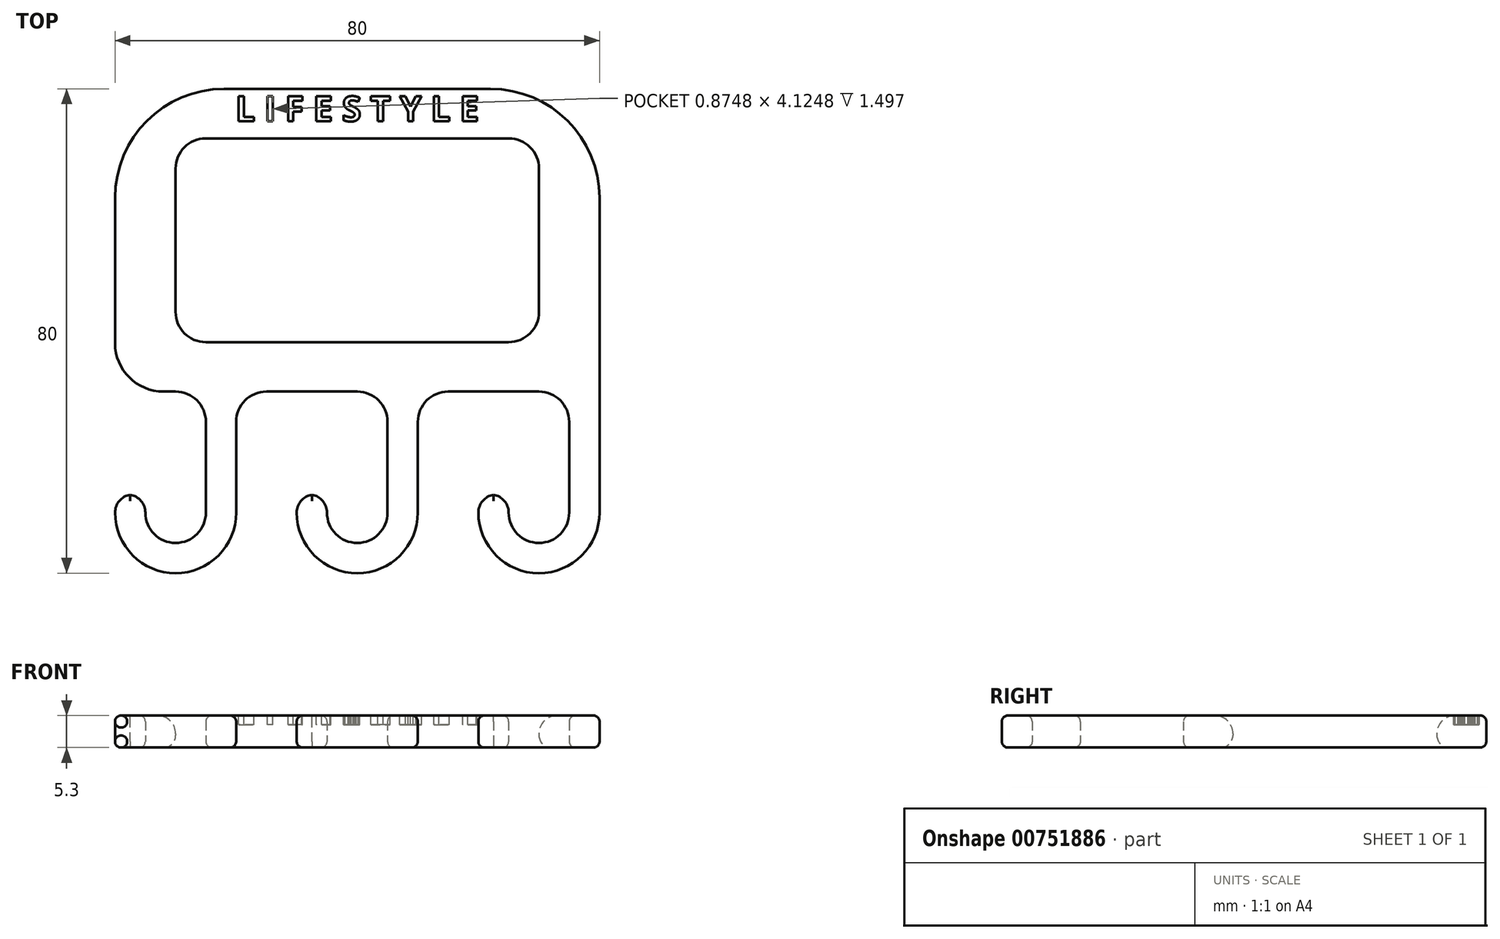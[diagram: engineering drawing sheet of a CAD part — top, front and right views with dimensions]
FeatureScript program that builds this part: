
annotation { "Feature Type Name" : "Feature", "Feature Type Description" : "" }
export const myFeature = defineFeature(function(context is Context, id is Id, definition is map)
    precondition{}
    {
        {
            var Q0;
            Q0=qCreatedBy(makeId("Top.planeOp"),FACE);
            var sketch = newSketch(context, id + "F0", { "sketchPlane" : qUnion([Q0])});
            skLineSegment(sketch, "E0.bottom", {"start": v(0, 0) * mm, "end": v(15, 0) * mm});
            skLineSegment(sketch, "E0.top", {"start": v(0, 50) * mm, "end": v(80, 50) * mm});
            skLineSegment(sketch, "E0.left", {"start": v(0, 0) * mm, "end": v(0, 50) * mm});
            skLineSegment(sketch, "E0.right", {"start": v(80, 0) * mm, "end": v(80, 50) * mm});
            skLineSegment(sketch, "E1", {"start": v(0, 0) * mm, "end": v(1.58, 0) * mm});
            skLineSegment(sketch, "E2", {"start": v(80, 50) * mm, "end": v(0, 0) * mm});
            skLineSegment(sketch, "E3.bottom", {"start": v(10, 41.84) * mm, "end": v(70, 41.84) * mm});
            skLineSegment(sketch, "E3.top", {"start": v(10, 8.16) * mm, "end": v(70, 8.16) * mm});
            skLineSegment(sketch, "E3.left", {"start": v(10, 41.84) * mm, "end": v(10, 8.16) * mm});
            skLineSegment(sketch, "E3.right", {"start": v(70, 41.84) * mm, "end": v(70, 8.16) * mm});
            skPoint(sketch, "E3.middle", {"position": v(40, 25) * mm});
            skLineSegment(sketch, "E4", {"start": v(45, 0) * mm, "end": v(45, -20) * mm});
            skLineSegment(sketch, "E5.bottom", {"start": v(35, 0) * mm, "end": v(45, 0) * mm});
            skLineSegment(sketch, "E5.right", {"start": v(50, 0) * mm, "end": v(50, -20) * mm});
            skPoint(sketch, "E5.middle", {"position": v(45, -10) * mm});
            skArc(sketch, "E6", {"start": v(30, -20) * mm, "mid": v(40, -30) * mm, "end": v(50, -20) * mm});
            skArc(sketch, "E7", {"start": v(35, -20) * mm, "mid": v(40, -25) * mm, "end": v(45, -20) * mm});
            skPoint(sketch, "E8.startSnap0", {"position": v(40, -30) * mm});
            skLineSegment(sketch, "E9.top", {"start": v(30, -17) * mm, "end": v(35, -17) * mm});
            skLineSegment(sketch, "E9.left", {"start": v(30, -20) * mm, "end": v(30, -17) * mm});
            skLineSegment(sketch, "E9.right", {"start": v(35, -20) * mm, "end": v(35, -17) * mm});
            skLineSegment(sketch, "E10", {"start": v(15, 0) * mm, "end": v(15, -20) * mm});
            skLineSegment(sketch, "E11.right", {"start": v(20, 0) * mm, "end": v(20, -20) * mm});
            skPoint(sketch, "E11.middle", {"position": v(15, -10) * mm});
            skArc(sketch, "E12", {"start": v(0, -20) * mm, "mid": v(10, -30) * mm, "end": v(20, -20) * mm});
            skArc(sketch, "E13", {"start": v(5, -20) * mm, "mid": v(10, -25) * mm, "end": v(15, -20) * mm});
            skPoint(sketch, "E14.startSnap0", {"position": v(10, -30) * mm});
            skLineSegment(sketch, "E15.top", {"start": v(0, -17) * mm, "end": v(5, -17) * mm});
            skLineSegment(sketch, "E15.left", {"start": v(0, -20) * mm, "end": v(0, -17) * mm});
            skLineSegment(sketch, "E15.right", {"start": v(5, -20) * mm, "end": v(5, -17) * mm});
            skLineSegment(sketch, "E16", {"start": v(75, 0) * mm, "end": v(75, -20) * mm});
            skLineSegment(sketch, "E17.right", {"start": v(80, 0) * mm, "end": v(80, -20) * mm});
            skPoint(sketch, "E17.middle", {"position": v(75, -10) * mm});
            skArc(sketch, "E18", {"start": v(60, -20) * mm, "mid": v(70, -30) * mm, "end": v(80, -20) * mm});
            skArc(sketch, "E19", {"start": v(65, -20) * mm, "mid": v(70, -25) * mm, "end": v(75, -20) * mm});
            skPoint(sketch, "E20.startSnap0", {"position": v(70, -30) * mm});
            skLineSegment(sketch, "E21.top", {"start": v(60, -17) * mm, "end": v(65, -17) * mm});
            skLineSegment(sketch, "E21.left", {"start": v(60, -20) * mm, "end": v(60, -17) * mm});
            skLineSegment(sketch, "E21.right", {"start": v(65, -20) * mm, "end": v(65, -17) * mm});
            skLineSegment(sketch, "E22.trimOffspring", {"start": v(20, 0) * mm, "end": v(45, 0) * mm});
            skLineSegment(sketch, "E23.trimOffspring", {"start": v(50, 0) * mm, "end": v(75, 0) * mm});
            skSolve(sketch);
        }
        {
            var Q0;
            Q0 = qSketchRegion(id + "F0", true);
            extrude(context, id + "F1", {"entities" : qUnion([Q0]), "depth" : 5.3 * mm, "offsetDistance" : 25 * mm});
        }
        {
            var Q0;
            Q0=makeQuery(id+"F1.opExtrude","SWEPT_EDGE",EDGE,{"disambiguationData":[OSD([sQuery(id+"F0.wireOp",EDGE,"E3.top"),sQuery(id+"F0.wireOp",EDGE,"E3.right")])]});
            var Q1;
            Q1=makeQuery(id+"F1.opExtrude","SWEPT_EDGE",EDGE,{"disambiguationData":[OSD([sQuery(id+"F0.wireOp",EDGE,"E3.top"),sQuery(id+"F0.wireOp",EDGE,"E3.left")])]});
            var Q2;
            Q2=makeQuery(id+"F1.opExtrude","SWEPT_EDGE",EDGE,{"disambiguationData":[OSD([sQuery(id+"F0.wireOp",EDGE,"E3.bottom"),sQuery(id+"F0.wireOp",EDGE,"E3.left")])]});
            var Q3;
            Q3=makeQuery(id+"F1.opExtrude","SWEPT_EDGE",EDGE,{"disambiguationData":[OSD([sQuery(id+"F0.wireOp",EDGE,"E3.bottom"),sQuery(id+"F0.wireOp",EDGE,"E3.right")])]});
            var Q4;
            Q4=makeQuery(id+"F1.opExtrude","SWEPT_EDGE",EDGE,{"disambiguationData":[OSD([sQuery(id+"F0.wireOp",EDGE,"E0.bottom"),sQuery(id+"F0.wireOp",EDGE,"E10")])]});
            var Q5;
            Q5=makeQuery(id+"F1.opExtrude","SWEPT_EDGE",EDGE,{"disambiguationData":[OSD([sQuery(id+"F0.wireOp",EDGE,"E4"),sQuery(id+"F0.wireOp",EDGE,"E22.trimOffspring")])]});
            fillet(context, id + "F2", {"entities" : qUnion([Q0, Q1, Q2, Q3, Q4, Q5]), "radius" : 5 * mm, "tangentPropagation" : true, "allowEdgeOverflow" : false});
        }
        {
            var Q0;
            Q0=makeQuery(id+"F1.opExtrude","SWEPT_EDGE",EDGE,{"disambiguationData":[OSD([sQuery(id+"F0.wireOp",EDGE,"E21.top"),sQuery(id+"F0.wireOp",EDGE,"E21.left")])]});
            var Q1;
            Q1=makeQuery(id+"F1.opExtrude","SWEPT_EDGE",EDGE,{"disambiguationData":[OSD([sQuery(id+"F0.wireOp",EDGE,"E21.top"),sQuery(id+"F0.wireOp",EDGE,"E21.right")])]});
            fillet(context, id + "F3", {"entities" : qUnion([Q0, Q1]), "radius" : 3 * mm, "tangentPropagation" : true, "allowEdgeOverflow" : false});
        }
        {
            var Q0;
            Q0=makeQuery(id+"F1.opExtrude","SWEPT_EDGE",EDGE,{"disambiguationData":[OSD([sQuery(id+"F0.wireOp",EDGE,"E9.top"),sQuery(id+"F0.wireOp",EDGE,"E9.right")])]});
            var Q1;
            Q1=makeQuery(id+"F1.opExtrude","SWEPT_EDGE",EDGE,{"disambiguationData":[OSD([sQuery(id+"F0.wireOp",EDGE,"E9.top"),sQuery(id+"F0.wireOp",EDGE,"E9.left")])]});
            fillet(context, id + "F4", {"entities" : qUnion([Q0, Q1]), "radius" : 3 * mm, "tangentPropagation" : true, "allowEdgeOverflow" : false});
        }
        {
            var Q0;
            Q0=makeQuery(id+"F1.opExtrude","SWEPT_EDGE",EDGE,{"disambiguationData":[OSD([sQuery(id+"F0.wireOp",EDGE,"E15.top"),sQuery(id+"F0.wireOp",EDGE,"E15.right")])]});
            var Q1;
            Q1=makeQuery(id+"F1.opExtrude","SWEPT_EDGE",EDGE,{"disambiguationData":[OSD([sQuery(id+"F0.wireOp",EDGE,"E15.top"),sQuery(id+"F0.wireOp",EDGE,"E15.left")])]});
            fillet(context, id + "F5", {"entities" : qUnion([Q0, Q1]), "radius" : 3 * mm, "tangentPropagation" : true, "allowEdgeOverflow" : false});
        }
        {
            var Q0;
            Q0=makeQuery(id+"F1.opExtrude","SWEPT_EDGE",EDGE,{"disambiguationData":[OSD([sQuery(id+"F0.wireOp",EDGE,"E0.left"),sQuery(id+"F0.wireOp",EDGE,"E1"),sQuery(id+"F0.wireOp",EDGE,"E2")])]});
            fillet(context, id + "F6", {"entities" : qUnion([Q0]), "radius" : 8 * mm, "tangentPropagation" : true, "allowEdgeOverflow" : false});
        }
        {
            var Q0;
            Q0=makeQuery(id+"F1.opExtrude","SWEPT_EDGE",EDGE,{"disambiguationData":[OSD([sQuery(id+"F0.wireOp",EDGE,"E0.top"),sQuery(id+"F0.wireOp",EDGE,"E0.left")])]});
            var Q1;
            Q1=makeQuery(id+"F1.opExtrude","SWEPT_EDGE",EDGE,{"disambiguationData":[OSD([sQuery(id+"F0.wireOp",EDGE,"E0.top"),sQuery(id+"F0.wireOp",EDGE,"E0.right"),sQuery(id+"F0.wireOp",EDGE,"E2")])]});
            fillet(context, id + "F7", {"entities" : qUnion([Q0, Q1]), "radius" : 18 * mm, "tangentPropagation" : true, "allowEdgeOverflow" : false});
        }
        {
            var Q0;
            Q0=makeQuery(id+"F1.opExtrude","SWEPT_EDGE",EDGE,{"disambiguationData":[OSD([sQuery(id+"F0.wireOp",EDGE,"E16"),sQuery(id+"F0.wireOp",EDGE,"E23.trimOffspring")])]});
            fillet(context, id + "F8", {"entities" : qUnion([Q0]), "radius" : 5 * mm, "tangentPropagation" : true, "allowEdgeOverflow" : false});
        }
        {
            var Q0;
            Q0=makeQuery(id+"F1.opExtrude","SWEPT_EDGE",EDGE,{"disambiguationData":[OSD([sQuery(id+"F0.wireOp",EDGE,"E11.right"),sQuery(id+"F0.wireOp",EDGE,"E22.trimOffspring")])]});
            var Q1;
            Q1=makeQuery(id+"F1.opExtrude","SWEPT_EDGE",EDGE,{"disambiguationData":[OSD([sQuery(id+"F0.wireOp",EDGE,"E5.right"),sQuery(id+"F0.wireOp",EDGE,"E23.trimOffspring")])]});
            fillet(context, id + "F9", {"entities" : qUnion([Q0, Q1]), "radius" : 5 * mm, "tangentPropagation" : true, "allowEdgeOverflow" : false});
        }
        {
            var Q0;
            Q0=makeQuery(id+"F1.opExtrude","CAP_EDGE",EDGE,{"disambiguationData":[OSD([sQuery(id+"F0.wireOp",EDGE,"E0.right"),sQuery(id+"F0.wireOp",EDGE,"E17.right")])],"isStart":false});
            var Q1;
            Q1=makeQuery(id+"F1.opExtrude","CAP_EDGE",EDGE,{"disambiguationData":[OSD([sQuery(id+"F0.wireOp",EDGE,"E5.right")])],"isStart":false});
            var Q2;
            Q2=makeQuery(id+"F1.opExtrude","CAP_EDGE",EDGE,{"disambiguationData":[OSD([sQuery(id+"F0.wireOp",EDGE,"E11.right")])],"isStart":false});
            fillet(context, id + "F10", {"entities" : qUnion([Q0, Q1, Q2]), "radius" : 1 * mm, "tangentPropagation" : true, "allowEdgeOverflow" : false});
        }
        {
            var Q0;
            Q0=makeQuery(id+"F1.opExtrude","CAP_EDGE",EDGE,{"disambiguationData":[OSD([sQuery(id+"F0.wireOp",EDGE,"E3.right")])],"isStart":true});
            fillet(context, id + "F11", {"entities" : qUnion([Q0]), "radius" : 2 * mm, "tangentPropagation" : true, "allowEdgeOverflow" : false});
        }
        {
            var Q0;
            Q0=makeQuery(id+"F1.opExtrude","CAP_EDGE",EDGE,{"disambiguationData":[OSD([sQuery(id+"F0.wireOp",EDGE,"E3.bottom")])],"isStart":false});
            fillet(context, id + "F12", {"entities" : qUnion([Q0]), "radius" : 3 * mm, "tangentPropagation" : true, "allowEdgeOverflow" : false});
        }
        {
            var Q0;
            Q0=makeQuery(id+"F1.opExtrude","CAP_EDGE",EDGE,{"disambiguationData":[OSD([sQuery(id+"F0.wireOp",EDGE,"E16")])],"isStart":true});
            var Q1;
            Q1=makeQuery(id+"F1.opExtrude","CAP_EDGE",EDGE,{"disambiguationData":[OSD([sQuery(id+"F0.wireOp",EDGE,"E4")])],"isStart":true});
            var Q2;
            Q2=makeQuery(id+"F1.opExtrude","CAP_EDGE",EDGE,{"disambiguationData":[OSD([sQuery(id+"F0.wireOp",EDGE,"E10")])],"isStart":true});
            fillet(context, id + "F13", {"entities" : qUnion([Q0, Q1, Q2]), "radius" : 1 * mm, "tangentPropagation" : true, "allowEdgeOverflow" : false});
        }
        {
            var Q0;
            Q0=makeQuery(id+"F1.opExtrude","CAP_FACE",FACE,{"disambiguationData":[OSD([sQuery(id+"F0.wireOp",EDGE,"E0.bottom"),sQuery(id+"F0.wireOp",EDGE,"E0.top"),sQuery(id+"F0.wireOp",EDGE,"E0.left"),sQuery(id+"F0.wireOp",EDGE,"E0.right"),sQuery(id+"F0.wireOp",EDGE,"E1"),sQuery(id+"F0.wireOp",EDGE,"E3.bottom"),sQuery(id+"F0.wireOp",EDGE,"E3.top"),sQuery(id+"F0.wireOp",EDGE,"E3.left"),sQuery(id+"F0.wireOp",EDGE,"E3.right"),sQuery(id+"F0.wireOp",EDGE,"E4"),sQuery(id+"F0.wireOp",EDGE,"E5.right"),sQuery(id+"F0.wireOp",EDGE,"E6"),sQuery(id+"F0.wireOp",EDGE,"E7"),sQuery(id+"F0.wireOp",EDGE,"E9.top"),sQuery(id+"F0.wireOp",EDGE,"E9.left"),sQuery(id+"F0.wireOp",EDGE,"E9.right"),sQuery(id+"F0.wireOp",EDGE,"E10"),sQuery(id+"F0.wireOp",EDGE,"E11.right"),sQuery(id+"F0.wireOp",EDGE,"E12"),sQuery(id+"F0.wireOp",EDGE,"E13"),sQuery(id+"F0.wireOp",EDGE,"E15.top"),sQuery(id+"F0.wireOp",EDGE,"E15.left"),sQuery(id+"F0.wireOp",EDGE,"E15.right"),sQuery(id+"F0.wireOp",EDGE,"E16"),sQuery(id+"F0.wireOp",EDGE,"E17.right"),sQuery(id+"F0.wireOp",EDGE,"E18"),sQuery(id+"F0.wireOp",EDGE,"E19"),sQuery(id+"F0.wireOp",EDGE,"E21.top"),sQuery(id+"F0.wireOp",EDGE,"E21.left"),sQuery(id+"F0.wireOp",EDGE,"E21.right"),sQuery(id+"F0.wireOp",EDGE,"E22.trimOffspring"),sQuery(id+"F0.wireOp",EDGE,"E23.trimOffspring")])],"isStart":false});
            var sketch = newSketch(context, id + "F14", { "sketchPlane" : qUnion([Q0])});
            skText(sketch, "E24", { "text": "L I F E S T Y L E ", "fontName": "OpenSans-Bold.ttf"});
            const initialGuessF14  = {"E24": [0.01988, 0.04465, 1, 0, 0.00416]};
            skSetInitialGuess(sketch, initialGuessF14);
            skSolve(sketch);
        }
        {
            var Q0;
            Q0 = qSketchRegion(id + "F14", true);
            extrude(context, id + "F15", {"entities" : qUnion([Q0]), "operationType" : NewBodyOperationType.REMOVE, "oppositeDirection" : true, "depth" : 1.5 * mm, "offsetDistance" : 25 * mm});
        }
    });
